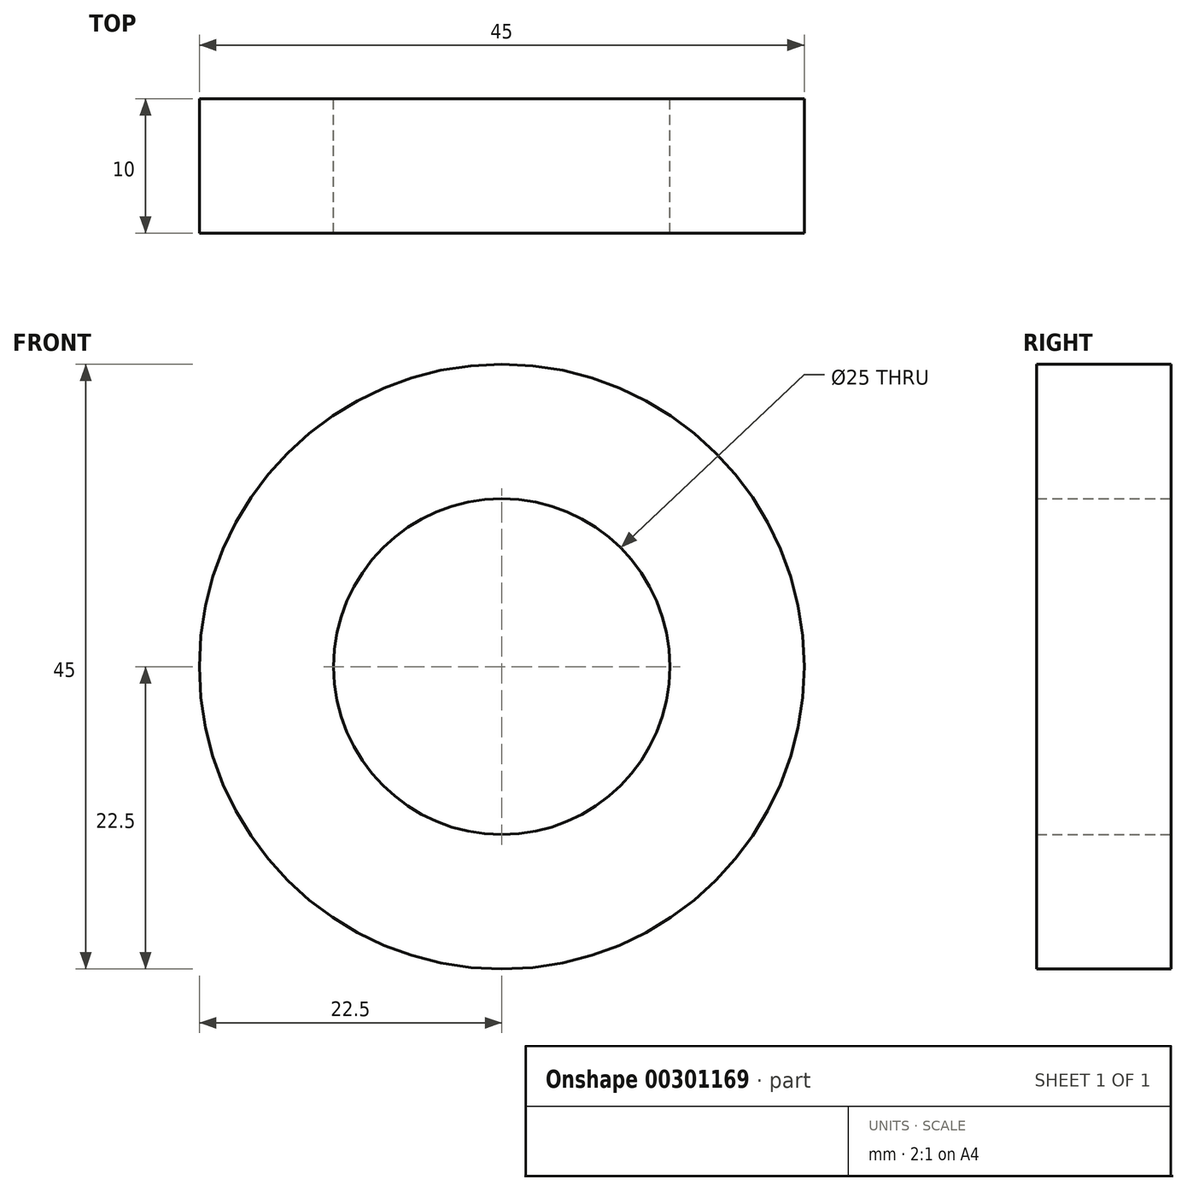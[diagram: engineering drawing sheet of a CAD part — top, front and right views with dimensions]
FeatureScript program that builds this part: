
annotation { "Feature Type Name" : "Feature", "Feature Type Description" : "" }
export const myFeature = defineFeature(function(context is Context, id is Id, definition is map)
    precondition{}
    {
        {
            var Q0;
            Q0=qCreatedBy(makeId("Front.planeOp"),FACE);
            var sketch = newSketch(context, id + "F0", { "sketchPlane" : qUnion([Q0])});
            skCircle(sketch, "E0", {"center": v(0, 0) * mm, "radius": 22.5 * mm});
            skCircle(sketch, "E1", {"center": v(0, 0) * mm, "radius": 12.5 * mm});
            skSolve(sketch);
        }
        {
            var Q0;
            Q0 = qSketchRegion(id + "F0", true);
            extrude(context, id + "F1", {"entities" : qUnion([Q0]), "depth" : 10 * mm});
        }
    });
